# Revit family: Trägerklemmung 35
name_source: partatom
category: HLS-Bauteile
revit_build: Autodesk Revit 2017 (Build: 20190507_1515(x64)
units: mm (PartAtom-declared; Revit-internal decimal feet)

## family parameters
Arbeitsebenenbasiert = Ja
Beim Laden mit Abzugskörper schneiden = Nein
Bemaßung runder Anschluss = Durchmesser verwenden
Gemeinsam genutzt = Ja
Immer vertikal = Nein
Raumberechnungspunkt = Nein
Teiletyp = Normal

## types (1)
- Trägerklemmung 35
    Achsabstand Schrauben = 70 mm
    Artikelnummer = 9999695
    Breite = 50 mm  [stored 0.164042 ft]
    EAN = 4250928448460
    Fabrikat = MEFA
    Firma = MEFA Befestigungs- und Montagesysteme GmbH
    Gewicht = 0.30 kg
    Gewicht pro Bauteil = 0.30 kg
    Kurztext1 = Trägerklemmung C-Profil 35
    Kurztext2 = für Profil 35/21, Stex 35/35 + 35/42
    Lochdurchmesser = 13 mm
    Länge = 100 mm  [stored 0.328084 ft]
    Material = Stahl
    Mengeneinheit = St
    Oberflaeche = galvanisch verzinkt
    Profiltyp = 35/21, Stex 35/35 + 35/42
    Vorgabe-Ansicht = 1219 mm
    max. zul. Last 35/21 (L = 400 mm) = 2 kN
    max. zul. Last 35/35 (L = 400 mm) = 2 kN
    max. zul. Last 35/42 (L = 400 mm) = 3 kN
    max. zul. Last Fx = 0.00 kN
    max. zul. Last Fz = 0.00 kN
    vpe = 20 St

note: [stored X ft] marks values corroborated as IEEE doubles in the binary element streams (Revit-internal decimal feet)

## geometry (parser evidence)
native form markers: Sweep x3
no freeform markers — native parametric forms only
